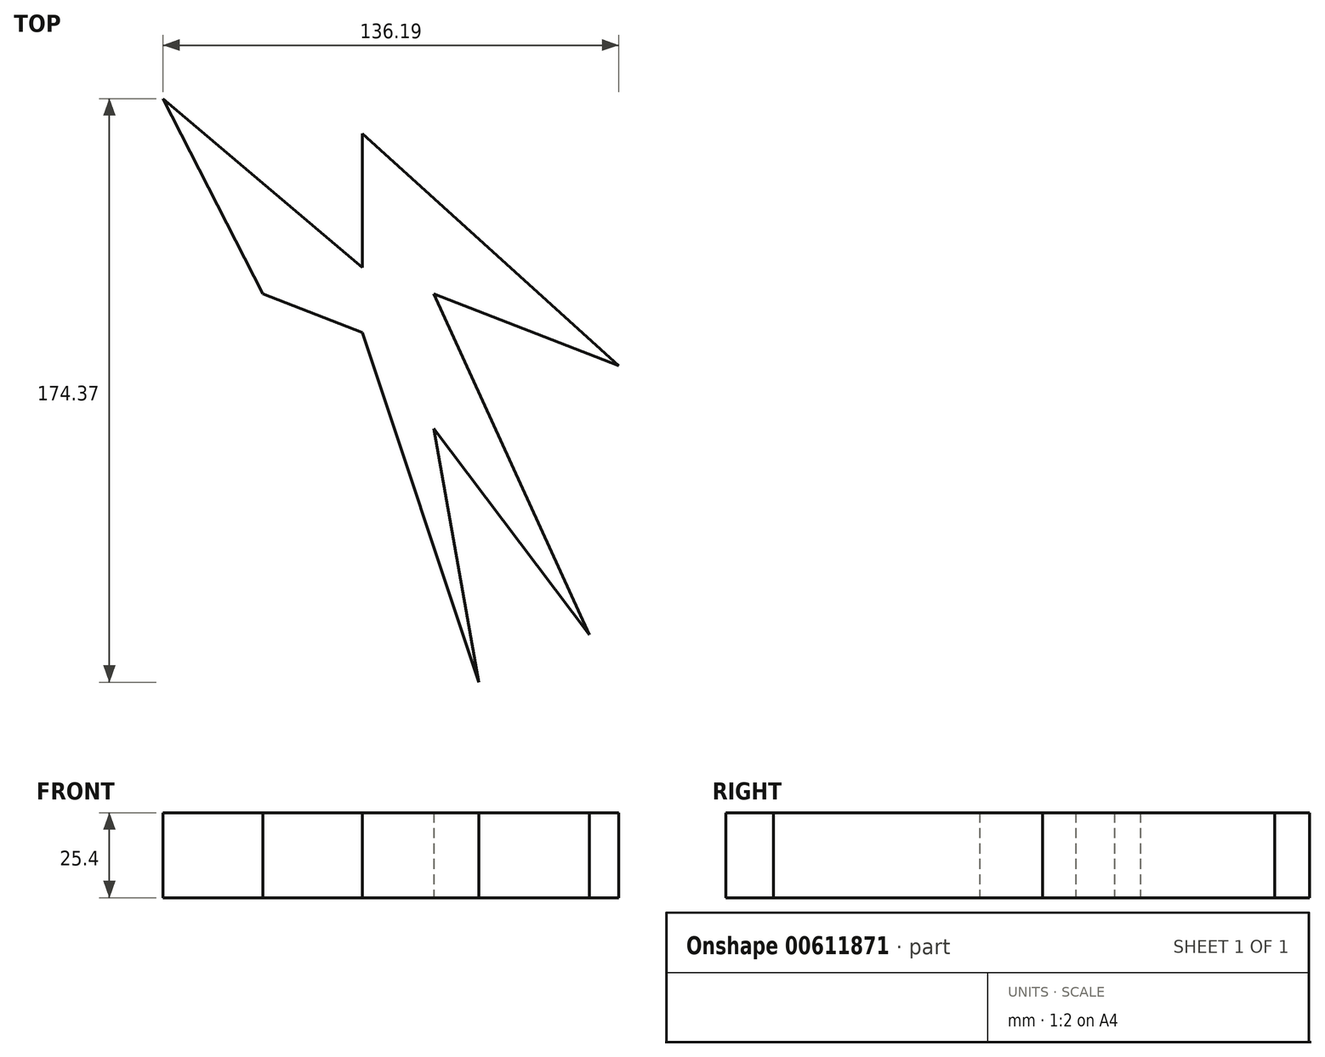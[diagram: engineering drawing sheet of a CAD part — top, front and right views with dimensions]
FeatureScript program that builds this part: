
annotation { "Feature Type Name" : "Feature", "Feature Type Description" : "" }
export const myFeature = defineFeature(function(context is Context, id is Id, definition is map)
    precondition{}
    {
        {
            var Q0;
            Q0=qCreatedBy(makeId("Top.planeOp"),FACE);
            var sketch = newSketch(context, id + "F0", { "sketchPlane" : qUnion([Q0])});
            skLineSegment(sketch, "E0", {"start": v(0, 0) * mm, "end": v(-13.45, 75.8) * mm});
            skLineSegment(sketch, "E1", {"start": v(-13.45, 75.8) * mm, "end": v(33.06, 14.17) * mm});
            skLineSegment(sketch, "E2", {"start": v(33.06, 14.17) * mm, "end": v(-13.45, 116.04) * mm});
            skLineSegment(sketch, "E3", {"start": v(-13.45, 116.04) * mm, "end": v(41.8, 94.6) * mm});
            skLineSegment(sketch, "E4", {"start": v(41.8, 94.6) * mm, "end": v(-34.85, 163.96) * mm});
            skLineSegment(sketch, "E5", {"start": v(-34.85, 163.96) * mm, "end": v(-34.85, 123.84) * mm});
            skLineSegment(sketch, "E6", {"start": v(-34.85, 123.84) * mm, "end": v(-94.4, 174.37) * mm});
            skLineSegment(sketch, "E7", {"start": v(-94.4, 174.37) * mm, "end": v(-64.56, 116.04) * mm});
            skLineSegment(sketch, "E8", {"start": v(-64.56, 116.04) * mm, "end": v(-34.85, 104.5) * mm});
            skLineSegment(sketch, "E9", {"start": v(-34.85, 104.5) * mm, "end": v(0, 0) * mm});
            skSolve(sketch);
        }
        {
            var Q0;
            Q0=makeQuery(id+"F0.imprint","IMPRINT",FACE,{"disambiguationData":[TD([[makeQuery(id+"F0.imprint","IMPRINT",EDGE,{"derivedFrom":sQuery(id+"F0.wireOp",EDGE,"E0")}),1.0]])]});
            extrude(context, id + "F1", {"entities" : qUnion([Q0]), "depth" : 25.4 * mm, "offsetDistance" : 25.4 * mm});
        }
    });
